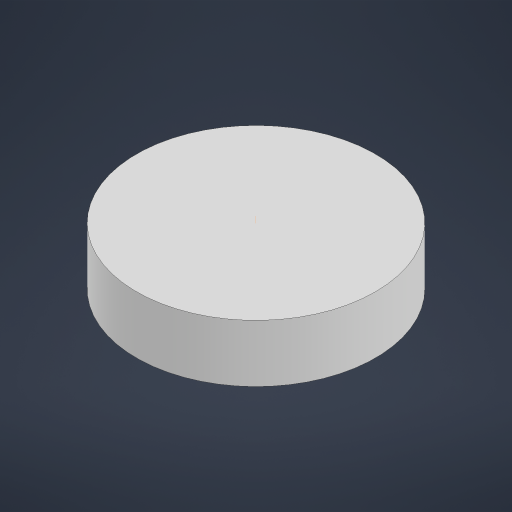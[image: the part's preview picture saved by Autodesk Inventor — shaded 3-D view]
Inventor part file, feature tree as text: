
AUTODESK INVENTOR PART (.ipt)
format: ipt  version: 2023 (Build 270158030, 158C)  size: 196,096 bytes
history: native  units: mm
features: sketch x3, extrude x2, shell x1, revolve x1, fillet x1
ambient origin geometry x8: Origin, YZ Plane, XZ Plane, XY Plane, X Axis, Y Axis, Z Axis, Center Point
bodies: Solid1 (feature_tree)
feature tree (8):
  extrude  "Extrusion1"  Depth=30.0mm
  extrude  "Extrusion2"  Depth=3.0mm TaperAngle=0.0deg
  shell  "Shell1"  Thickness=1.5mm
  revolve  "Revolution1"  Angle=90.0deg
  fillet  "Fillet1"  Radius=1.5mm
  sketch  "Sketch1"  dims[d0=11.7mm d1=30.0mm]
  sketch  "Sketch2"  dims[d2=4.2mm d3=0.0mm d4=3.0mm d5=0.0mm d6=1.5mm]
  sketch  "Sketch3"  dims[d7=4.0mm d8=90.0deg d9=1.5mm]
